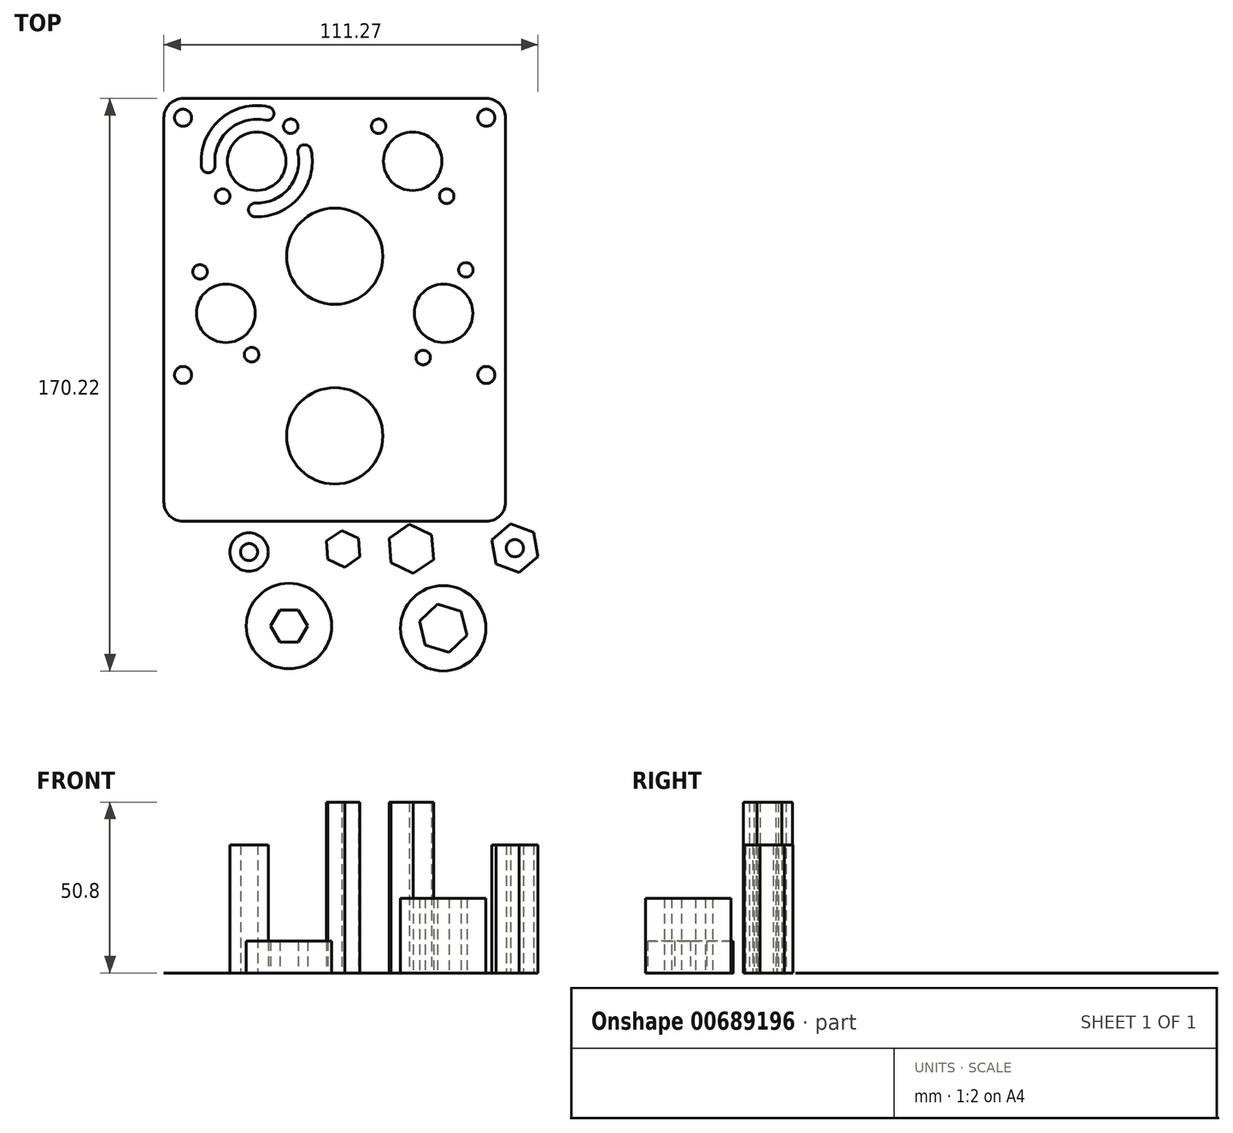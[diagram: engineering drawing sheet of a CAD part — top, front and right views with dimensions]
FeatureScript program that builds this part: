
annotation { "Feature Type Name" : "Feature", "Feature Type Description" : "" }
export const myFeature = defineFeature(function(context is Context, id is Id, definition is map)
    precondition{}
    {
        {
            var Q0;
            Q0=qCreatedBy(makeId("Top.planeOp"),FACE);
            var sketch = newSketch(context, id + "F0", { "sketchPlane" : qUnion([Q0])});
            skCircle(sketch, "E0", {"center": v(-55.1, 96.88) * mm, "radius": 4.76 * mm, "construction": true});
            skCircle(sketch, "E1", {"center": v(-31.92, 68.63) * mm, "radius": 31.79 * mm, "construction": true});
            skCircle(sketch, "E2", {"center": v(-8.73, 96.88) * mm, "radius": 4.76 * mm, "construction": true});
            skCircle(sketch, "E3", {"center": v(-31.92, 68.63) * mm, "radius": 15.24 * mm, "construction": true});
            skCircle(sketch, "E4", {"center": v(-31.92, 15.21) * mm, "radius": 38.1 * mm, "construction": true});
            skCircle(sketch, "E5", {"center": v(-64.3, 51.67) * mm, "radius": 4.76 * mm, "construction": true});
            skCircle(sketch, "E6", {"center": v(0.46, 51.67) * mm, "radius": 4.76 * mm, "construction": true});
            skCircle(sketch, "E7", {"center": v(-55.1, 96.88) * mm, "radius": 8.71 * mm});
            skCircle(sketch, "E8", {"center": v(-64.3, 51.67) * mm, "radius": 8.71 * mm});
            skCircle(sketch, "E9", {"center": v(-8.73, 96.88) * mm, "radius": 8.71 * mm});
            skCircle(sketch, "E10", {"center": v(0.46, 51.67) * mm, "radius": 8.71 * mm});
            skCircle(sketch, "E11", {"center": v(-55.1, 96.88) * mm, "radius": 14.5 * mm, "construction": true});
            skCircle(sketch, "E12", {"center": v(-64.3, 51.67) * mm, "radius": 14.5 * mm, "construction": true});
            skCircle(sketch, "E13", {"center": v(-8.73, 96.88) * mm, "radius": 14.5 * mm, "construction": true});
            skCircle(sketch, "E14", {"center": v(0.46, 51.67) * mm, "radius": 14.5 * mm, "construction": true});
            skCircle(sketch, "E15", {"center": v(-31.92, 68.63) * mm, "radius": 14.33 * mm});
            skCircle(sketch, "E16", {"center": v(-31.92, 15.21) * mm, "radius": 14.33 * mm});
            skLineSegment(sketch, "E17", {"start": v(-55.1, 96.88) * mm, "end": v(-8.73, 96.88) * mm, "construction": true});
            skLineSegment(sketch, "E18", {"start": v(-64.3, 51.67) * mm, "end": v(0.46, 51.67) * mm, "construction": true});
            skCircle(sketch, "E19", {"center": v(-45, 107.28) * mm, "radius": 2.16 * mm});
            skCircle(sketch, "E20", {"center": v(-65.21, 86.49) * mm, "radius": 2.16 * mm});
            skCircle(sketch, "E21", {"center": v(-18.84, 107.28) * mm, "radius": 2.16 * mm});
            skCircle(sketch, "E22", {"center": v(1.38, 86.49) * mm, "radius": 2.16 * mm});
            skLineSegment(sketch, "E23", {"start": v(-65.21, 86.49) * mm, "end": v(-45, 107.28) * mm, "construction": true});
            skLineSegment(sketch, "E24", {"start": v(-18.84, 107.28) * mm, "end": v(1.38, 86.49) * mm, "construction": true});
            skLineSegment(sketch, "E25", {"start": v(-31.92, 114.3) * mm, "end": v(-31.92, -10.19) * mm, "construction": true});
            skLineSegment(sketch, "E26", {"start": v(-82.72, 51.67) * mm, "end": v(-82.72, -10.19) * mm});
            skLineSegment(sketch, "E27", {"start": v(-82.72, -10.19) * mm, "end": v(18.88, -10.19) * mm});
            skLineSegment(sketch, "E28", {"start": v(18.88, -10.19) * mm, "end": v(18.88, 51.67) * mm});
            skLineSegment(sketch, "E29", {"start": v(18.88, 51.67) * mm, "end": v(18.88, 115.54) * mm});
            skLineSegment(sketch, "E30", {"start": v(18.88, 115.54) * mm, "end": v(-82.72, 115.54) * mm});
            skLineSegment(sketch, "E31", {"start": v(-82.72, 115.54) * mm, "end": v(-82.72, 51.67) * mm});
            skCircle(sketch, "E32", {"center": v(-77, 109.83) * mm, "radius": 2.54 * mm});
            skCircle(sketch, "E33", {"center": v(13.17, 109.83) * mm, "radius": 2.54 * mm});
            skCircle(sketch, "E34", {"center": v(-77, 33.33) * mm, "radius": 2.54 * mm});
            skCircle(sketch, "E35", {"center": v(13.17, 33.33) * mm, "radius": 2.54 * mm});
            skCircle(sketch, "E36", {"center": v(-64.3, 51.67) * mm, "radius": 22.53 * mm, "construction": true});
            skCircle(sketch, "E37", {"center": v(0.46, 51.67) * mm, "radius": 22.53 * mm, "construction": true});
            skCircle(sketch, "E38", {"center": v(-8.73, 96.88) * mm, "radius": 22.53 * mm, "construction": true});
            skCircle(sketch, "E39", {"center": v(-55.1, 96.88) * mm, "radius": 22.53 * mm, "construction": true});
            skPoint(sketch, "E40.middle", {"position": v(-31.92, 71.58) * mm});
            skCircle(sketch, "E41", {"center": v(-56.62, 39.36) * mm, "radius": 2.16 * mm});
            skCircle(sketch, "E42", {"center": v(-71.97, 63.98) * mm, "radius": 2.16 * mm});
            skLineSegment(sketch, "E43", {"start": v(-71.97, 63.98) * mm, "end": v(-56.62, 39.36) * mm, "construction": true});
            skCircle(sketch, "E44", {"center": v(7.08, 64.58) * mm, "radius": 2.16 * mm});
            skCircle(sketch, "E45", {"center": v(-5.6, 38.5) * mm, "radius": 2.16 * mm});
            skLineSegment(sketch, "E46", {"start": v(-5.6, 38.5) * mm, "end": v(7.08, 64.58) * mm, "construction": true});
            skArc(sketch, "E47.trimOffspring", {"start": v(-55.54, 82.39) * mm, "mid": v(-44.03, 87.52) * mm, "end": v(-40.88, 99.73) * mm});
            skArc(sketch, "E48.trimOffspring", {"start": v(-52.01, 111.05) * mm, "mid": v(-64.74, 107.72) * mm, "end": v(-69.54, 95.47) * mm});
            skArc(sketch, "E49.0.startCap", {"start": v(-51.58, 113.04) * mm, "mid": v(-50.03, 110.62) * mm, "end": v(-52.44, 109.07) * mm});
            skArc(sketch, "E49.0.endCap", {"start": v(-67.51, 95.67) * mm, "mid": v(-69.34, 93.45) * mm, "end": v(-71.56, 95.27) * mm});
            skArc(sketch, "E49.0.left", {"start": v(-52.44, 109.07) * mm, "mid": v(-63.39, 106.2) * mm, "end": v(-67.51, 95.67) * mm});
            skArc(sketch, "E49.0.right", {"start": v(-51.58, 113.04) * mm, "mid": v(-66.09, 109.24) * mm, "end": v(-71.56, 95.27) * mm});
            skArc(sketch, "E49.1.startCap", {"start": v(-55.6, 80.36) * mm, "mid": v(-57.57, 82.45) * mm, "end": v(-55.48, 84.42) * mm});
            skArc(sketch, "E49.1.endCap", {"start": v(-42.87, 99.33) * mm, "mid": v(-41.28, 101.72) * mm, "end": v(-38.89, 100.13) * mm});
            skArc(sketch, "E49.1.left", {"start": v(-55.48, 84.42) * mm, "mid": v(-45.58, 88.83) * mm, "end": v(-42.87, 99.33) * mm});
            skArc(sketch, "E49.1.right", {"start": v(-55.6, 80.36) * mm, "mid": v(-42.47, 86.2) * mm, "end": v(-38.89, 100.13) * mm});
            skSolve(sketch);
        }
        {
            var Q0;
            Q0=makeQuery(id+"F0.imprint","IMPRINT",FACE,{"disambiguationData":[TD([[makeQuery(id+"F0.imprint","IMPRINT",EDGE,{"derivedFrom":sQuery(id+"F0.wireOp",EDGE,"E7")}),-1.0]])]});
            extrude(context, id + "F1", {"entities" : qUnion([Q0]), "depth" : 1 / 101.6 * mm, "offsetDistance" : 25.4 * mm});
        }
        {
            var Q0;
            Q0=qCreatedBy(makeId("Top.planeOp"),FACE);
            var sketch = newSketch(context, id + "F2", { "sketchPlane" : qUnion([Q0])});
            skCircle(sketch, "E50", {"center": v(-57.39, -19.33) * mm, "radius": 5.72 * mm});
            skCircle(sketch, "E51", {"center": v(-57.39, -19.33) * mm, "radius": 2.54 * mm});
            skSolve(sketch);
        }
        {
            var Q0;
            Q0=makeQuery(id+"F2.imprint","IMPRINT",FACE,{"disambiguationData":[TD([[makeQuery(id+"F2.imprint","IMPRINT",EDGE,{"derivedFrom":sQuery(id+"F2.wireOp",EDGE,"E50")}),1.0]])]});
            extrude(context, id + "F3", {"entities" : qUnion([Q0]), "depth" : 38.1 * mm, "offsetDistance" : 25.4 * mm});
        }
        {
            var Q0;
            Q0=qCreatedBy(makeId("Top.planeOp"),FACE);
            var sketch = newSketch(context, id + "F4", { "sketchPlane" : qUnion([Q0])});
            skCircle(sketch, "E52.cCircle", {"center": v(-29.38, -18.38) * mm, "radius": 4.76 * mm, "construction": true});
            skLineSegment(sketch, "E52.0", {"start": v(-24.42, -20.75) * mm, "end": v(-28.95, -23.86) * mm});
            skLineSegment(sketch, "E52.1", {"start": v(-28.95, -23.86) * mm, "end": v(-33.92, -21.5) * mm});
            skLineSegment(sketch, "E52.2", {"start": v(-33.92, -21.5) * mm, "end": v(-34.35, -16.01) * mm});
            skLineSegment(sketch, "E52.3", {"start": v(-34.35, -16.01) * mm, "end": v(-29.82, -12.9) * mm});
            skLineSegment(sketch, "E52.4", {"start": v(-29.82, -12.9) * mm, "end": v(-24.85, -15.26) * mm});
            skLineSegment(sketch, "E52.5", {"start": v(-24.85, -15.26) * mm, "end": v(-24.42, -20.75) * mm});
            skPoint(sketch, "E52.0.midPoint", {"position": v(-26.69, -22.3) * mm});
            skCircle(sketch, "E53.cCircle", {"center": v(-9.14, -18.38) * mm, "radius": 6.35 * mm, "construction": true});
            skLineSegment(sketch, "E53.0", {"start": v(-2.52, -21.53) * mm, "end": v(-8.56, -25.69) * mm});
            skLineSegment(sketch, "E53.1", {"start": v(-8.56, -25.69) * mm, "end": v(-15.18, -22.53) * mm});
            skLineSegment(sketch, "E53.2", {"start": v(-15.18, -22.53) * mm, "end": v(-15.76, -15.22) * mm});
            skLineSegment(sketch, "E53.3", {"start": v(-15.76, -15.22) * mm, "end": v(-9.72, -11.07) * mm});
            skLineSegment(sketch, "E53.4", {"start": v(-9.72, -11.07) * mm, "end": v(-3.1, -14.22) * mm});
            skLineSegment(sketch, "E53.5", {"start": v(-3.1, -14.22) * mm, "end": v(-2.52, -21.53) * mm});
            skPoint(sketch, "E53.0.midPoint", {"position": v(-5.54, -23.61) * mm});
            skSolve(sketch);
        }
        {
            var Q0;
            Q0=makeQuery(id+"F4.imprint","IMPRINT",FACE,{"disambiguationData":[TD([[makeQuery(id+"F4.imprint","IMPRINT",EDGE,{"derivedFrom":sQuery(id+"F4.wireOp",EDGE,"E52.0")}),-1.0]])]});
            var Q1;
            Q1=makeQuery(id+"F4.imprint","IMPRINT",FACE,{"disambiguationData":[TD([[makeQuery(id+"F4.imprint","IMPRINT",EDGE,{"derivedFrom":sQuery(id+"F4.wireOp",EDGE,"E53.0")}),-1.0]])]});
            extrude(context, id + "F5", {"entities" : qUnion([Q0, Q1]), "depth" : 50.8 * mm, "offsetDistance" : 25.4 * mm});
        }
        {
            var Q0;
            Q0=qCreatedBy(makeId("Top.planeOp"),FACE);
            var sketch = newSketch(context, id + "F6", { "sketchPlane" : qUnion([Q0])});
            skCircle(sketch, "E54", {"center": v(-45.5, -41.33) * mm, "radius": 12.7 * mm});
            skCircle(sketch, "E55.cCircle", {"center": v(-45.5, -41.33) * mm, "radius": 4.76 * mm, "construction": true});
            skLineSegment(sketch, "E55.0", {"start": v(-42.76, -46.1) * mm, "end": v(-48.26, -46.1) * mm});
            skLineSegment(sketch, "E55.1", {"start": v(-48.26, -46.1) * mm, "end": v(-51, -41.33) * mm});
            skLineSegment(sketch, "E55.2", {"start": v(-51, -41.33) * mm, "end": v(-48.26, -36.57) * mm});
            skLineSegment(sketch, "E55.3", {"start": v(-48.26, -36.57) * mm, "end": v(-42.76, -36.57) * mm});
            skLineSegment(sketch, "E55.4", {"start": v(-42.76, -36.57) * mm, "end": v(-40.01, -41.33) * mm});
            skLineSegment(sketch, "E55.5", {"start": v(-40.01, -41.33) * mm, "end": v(-42.76, -46.1) * mm});
            skPoint(sketch, "E55.0.midPoint", {"position": v(-45.5, -46.1) * mm});
            skSolve(sketch);
        }
        {
            var Q0;
            Q0=makeQuery(id+"F6.imprint","IMPRINT",FACE,{"disambiguationData":[TD([[makeQuery(id+"F6.imprint","IMPRINT",EDGE,{"derivedFrom":sQuery(id+"F6.wireOp",EDGE,"E54")}),1.0]])]});
            extrude(context, id + "F7", {"entities" : qUnion([Q0]), "depth" : 9.52 * mm, "offsetDistance" : 25.4 * mm});
        }
        {
            var Q0;
            Q0=qCreatedBy(makeId("Top.planeOp"),FACE);
            var sketch = newSketch(context, id + "F8", { "sketchPlane" : qUnion([Q0])});
            skCircle(sketch, "E56", {"center": v(0.35, -41.98) * mm, "radius": 12.7 * mm});
            skCircle(sketch, "E57.cCircle", {"center": v(0.35, -41.98) * mm, "radius": 6.35 * mm, "construction": true});
            skLineSegment(sketch, "E57.0", {"start": v(7.38, -44.07) * mm, "end": v(2.05, -49.12) * mm});
            skLineSegment(sketch, "E57.1", {"start": v(2.05, -49.12) * mm, "end": v(-4.97, -47.02) * mm});
            skLineSegment(sketch, "E57.2", {"start": v(-4.97, -47.02) * mm, "end": v(-6.68, -39.9) * mm});
            skLineSegment(sketch, "E57.3", {"start": v(-6.68, -39.9) * mm, "end": v(-1.35, -34.85) * mm});
            skLineSegment(sketch, "E57.4", {"start": v(-1.35, -34.85) * mm, "end": v(5.68, -36.94) * mm});
            skLineSegment(sketch, "E57.5", {"start": v(5.68, -36.94) * mm, "end": v(7.38, -44.07) * mm});
            skPoint(sketch, "E57.0.midPoint", {"position": v(4.72, -46.6) * mm});
            skSolve(sketch);
        }
        {
            var Q0;
            Q0=makeQuery(id+"F8.imprint","IMPRINT",FACE,{"disambiguationData":[TD([[makeQuery(id+"F8.imprint","IMPRINT",EDGE,{"derivedFrom":sQuery(id+"F8.wireOp",EDGE,"E56")}),1.0]])]});
            extrude(context, id + "F9", {"entities" : qUnion([Q0]), "depth" : 22.22 * mm, "offsetDistance" : 25.4 * mm});
        }
        {
            var Q0;
            Q0=makeQuery(id+"F1.opExtrude","SWEPT_EDGE",EDGE,{"disambiguationData":[OSD([sQuery(id+"F0.wireOp",EDGE,"E30"),sQuery(id+"F0.wireOp",EDGE,"E31")])]});
            var Q1;
            Q1=makeQuery(id+"F1.opExtrude","SWEPT_EDGE",EDGE,{"disambiguationData":[OSD([sQuery(id+"F0.wireOp",EDGE,"E29"),sQuery(id+"F0.wireOp",EDGE,"E30")])]});
            var Q2;
            Q2=makeQuery(id+"F1.opExtrude","SWEPT_EDGE",EDGE,{"disambiguationData":[OSD([sQuery(id+"F0.wireOp",EDGE,"E27"),sQuery(id+"F0.wireOp",EDGE,"E28")])]});
            var Q3;
            Q3=makeQuery(id+"F1.opExtrude","SWEPT_EDGE",EDGE,{"disambiguationData":[OSD([sQuery(id+"F0.wireOp",EDGE,"E26"),sQuery(id+"F0.wireOp",EDGE,"E27")])]});
            fillet(context, id + "F10", {"entities" : qUnion([Q0, Q1, Q2, Q3]), "radius" : 5.7 * mm, "tangentPropagation" : true, "allowEdgeOverflow" : false});
        }
        {
            var Q0;
            Q0=qCreatedBy(makeId("Top.planeOp"),FACE);
            var sketch = newSketch(context, id + "F11", { "sketchPlane" : qUnion([Q0])});
            skCircle(sketch, "E58", {"center": v(21.65, -18.19) * mm, "radius": 2.55 * mm});
            skCircle(sketch, "E59.cCircle", {"center": v(21.65, -18.19) * mm, "radius": 6.35 * mm, "construction": true});
            skLineSegment(sketch, "E59.0", {"start": v(28.55, -20.68) * mm, "end": v(22.93, -25.4) * mm});
            skLineSegment(sketch, "E59.1", {"start": v(22.93, -25.4) * mm, "end": v(16.04, -22.9) * mm});
            skLineSegment(sketch, "E59.2", {"start": v(16.04, -22.9) * mm, "end": v(14.76, -15.69) * mm});
            skLineSegment(sketch, "E59.3", {"start": v(14.76, -15.69) * mm, "end": v(20.37, -10.97) * mm});
            skLineSegment(sketch, "E59.4", {"start": v(20.37, -10.97) * mm, "end": v(27.26, -13.46) * mm});
            skLineSegment(sketch, "E59.5", {"start": v(27.26, -13.46) * mm, "end": v(28.55, -20.68) * mm});
            skPoint(sketch, "E59.0.midPoint", {"position": v(25.74, -23.04) * mm});
            skSolve(sketch);
        }
        {
            var Q0;
            Q0=makeQuery(id+"F11.imprint","IMPRINT",FACE,{"disambiguationData":[TD([[makeQuery(id+"F11.imprint","IMPRINT",EDGE,{"derivedFrom":sQuery(id+"F11.wireOp",EDGE,"E58")}),-1.0]])]});
            extrude(context, id + "F12", {"entities" : qUnion([Q0]), "depth" : 38.1 * mm, "offsetDistance" : 25.4 * mm});
        }
    });
